# Revit family: vvvv
name_source: partatom
category: Plumbing Fixtures
units: mm (PartAtom-declared; Revit-internal decimal feet)

## family parameters
Cut with Voids When Loaded = No
Host = Face
OmniClass Number = 23.45.05.14.99
OmniClass Title = Other Sanitary Washing Plumbing Fixtures
Part Type = Normal
Room Calculation Point = No
Round Connector Dimension = Use Diameter
Shared = No

## types (4) — shared parameters
Apparent Load = 0 VA
Assembly Code = D2020300
CW Connection = Yes
Centerline of Supply from Top of Fixture = 11.5 "
Centerline of Supply to Centerline of Valve = 4.75 "
Current = 0 A
Edition number = 1
HW Connection = No
Height = 13.5 "
Keynote = 15410
Manufacturer = Sloan Valve
Number of Poles = 3
Operating Water Pressure = 15 – 80 PSI (103 – 552 kPa)
Power Factor = 0.8
Product Material = Sloan Valve - Finish - Polished Chrome
Product data url = https://www.bimobject.com
URL = www.sloanvalve.com
Valve Pressure Drop = 0.00 psi
Vent Connection = No
Waste Connection = No
Water Inlet Connection Diameter = 1"
zero-valued in all types: CWFU, Default Elevation, HWFU, WFU

## per-type parameters (varying)
| type | Description | Flush Rate | Hardwired | Number | Part Number | Voltage |
| REGAL 111 SFSM-1.28 | 1.28 gpf, Polished Chrome Finish, Fixture Connection Top Spud, Single
Flush, Battery, Regal® Exposed Sensor Water Closet Flushometer. | 1.28 gpf (4.8 Lpf) | No | 2 | 3080058 | 0 V |
| REGAL 111 SFSM-1.28-HW | 1.28 gpf, Polished Chrome Finish, Fixture Connection Top Spud, Single
Flush, Hardwired, Regal® Exposed Sensor Water Closet Flushometer. | 1.28 gpf (4.8 Lpf) | Yes | 3 | 3080052 | 6 V |
| REGAL 111 SFSM-1.6 | 1.6 gpf, Polished Chrome Finish, Fixture Connection Top Spud, Single
Flush, Battery, Regal® Exposed Sensor Water Closet Flushometer. | 1.6 gpf (6.0 Lpf) | No | 2 | 3980095 | 0 V |
| REGAL 111 SFSM-1.6-HW | 1.6 gpf, Polished Chrome Finish, Fixture Connection Top Spud, Single
Flush, Hardwired, Regal® Exposed Sensor Water Closet Flushometer. | 1.6 gpf (6.0 Lpf) | Yes | 3 | 3980096 | 6 V |

note: column(s) folded — value = type name in every type: Model

## geometry (parser evidence)
native form markers: Sweep x7
no freeform markers — native parametric forms only
